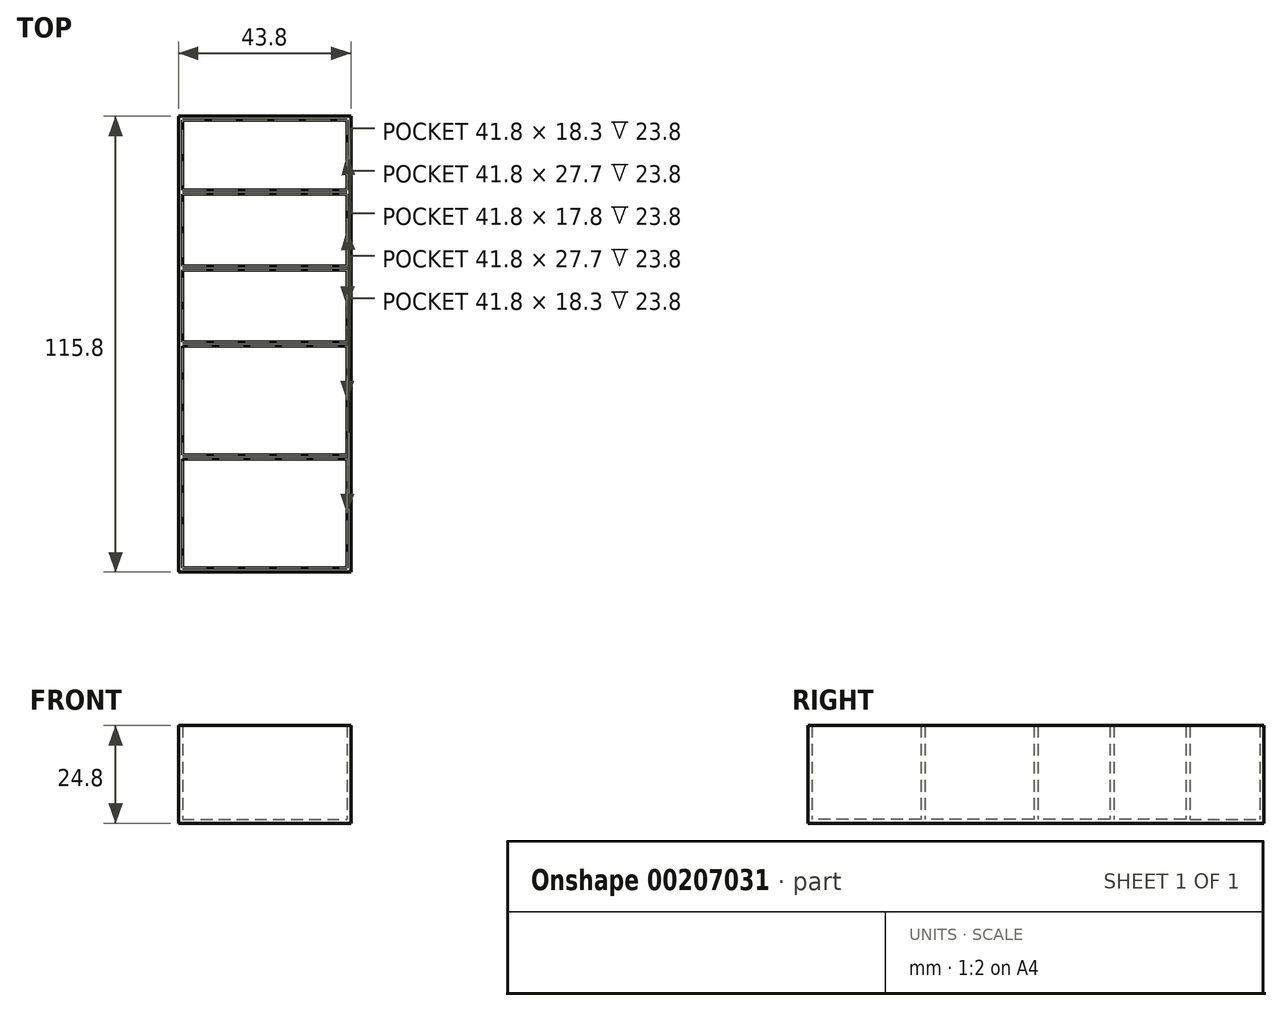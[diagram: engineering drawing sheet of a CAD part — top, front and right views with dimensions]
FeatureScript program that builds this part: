
annotation { "Feature Type Name" : "Feature", "Feature Type Description" : "" }
export const myFeature = defineFeature(function(context is Context, id is Id, definition is map)
    precondition{}
    {
        {
            var Q0;
            Q0=qCreatedBy(makeId("Top.planeOp"),FACE);
            var sketch = newSketch(context, id + "F0", { "sketchPlane" : qUnion([Q0])});
            skLineSegment(sketch, "E0.bottom", {"start": v(0, 0) * mm, "end": v(43.8, 0) * mm});
            skLineSegment(sketch, "E0.top", {"start": v(0, -115.8) * mm, "end": v(43.8, -115.8) * mm});
            skLineSegment(sketch, "E0.left", {"start": v(0, 0) * mm, "end": v(0, -115.8) * mm});
            skLineSegment(sketch, "E0.right", {"start": v(43.8, 0) * mm, "end": v(43.8, -115.8) * mm});
            skSolve(sketch);
        }
        {
            var Q0;
            Q0=makeQuery(id+"F0.imprint","IMPRINT",FACE,{"disambiguationData":[TD([[makeQuery(id+"F0.imprint","IMPRINT",EDGE,{"derivedFrom":sQuery(id+"F0.wireOp",EDGE,"E0.bottom")}),-1.0]])]});
            extrude(context, id + "F1", {"entities" : qUnion([Q0]), "depth" : 1 * mm});
        }
        {
            var Q0;
            Q0=makeQuery(id+"F1.opExtrude","CAP_FACE",FACE,{"disambiguationData":[OSD([sQuery(id+"F0.wireOp",EDGE,"E0.bottom"),sQuery(id+"F0.wireOp",EDGE,"E0.top"),sQuery(id+"F0.wireOp",EDGE,"E0.left"),sQuery(id+"F0.wireOp",EDGE,"E0.right")])],"isStart":false});
            var sketch = newSketch(context, id + "F2", { "sketchPlane" : qUnion([Q0])});
            skLineSegment(sketch, "E1.top", {"start": v(0, -115.8) * mm, "end": v(43.8, -115.8) * mm});
            skLineSegment(sketch, "E2.0", {"start": v(1, -18.8) * mm, "end": v(42.8, -18.8) * mm});
            skLineSegment(sketch, "E3.0", {"start": v(1, -19.8) * mm, "end": v(42.8, -19.8) * mm});
            skLineSegment(sketch, "E4.0", {"start": v(1, -39.1) * mm, "end": v(42.8, -39.1) * mm});
            skLineSegment(sketch, "E5.0", {"start": v(1, -38.1) * mm, "end": v(42.8, -38.1) * mm});
            skLineSegment(sketch, "E6.0", {"start": v(1, -57.4) * mm, "end": v(42.8, -57.4) * mm});
            skLineSegment(sketch, "E7.0", {"start": v(1, -58.4) * mm, "end": v(42.8, -58.4) * mm});
            skLineSegment(sketch, "E8.0", {"start": v(42.8, -1) * mm, "end": v(1, -1) * mm});
            skLineSegment(sketch, "E8.2", {"start": v(1, -114.8) * mm, "end": v(42.8, -114.8) * mm});
            skLineSegment(sketch, "E8.3", {"start": v(1, -1) * mm, "end": v(1, -18.8) * mm});
            skLineSegment(sketch, "E9.trimOffspring", {"start": v(1, -87.35) * mm, "end": v(1, -114.8) * mm});
            skLineSegment(sketch, "E10.trimOffspring", {"start": v(1, -58.4) * mm, "end": v(1, -86.35) * mm});
            skLineSegment(sketch, "E11.trimOffspring", {"start": v(42.8, -57.4) * mm, "end": v(42.8, -39.1) * mm});
            skLineSegment(sketch, "E12.trimOffspring", {"start": v(42.8, -38.1) * mm, "end": v(42.8, -19.8) * mm});
            skLineSegment(sketch, "E13.trimOffspring", {"start": v(1, -39.1) * mm, "end": v(1, -57.4) * mm});
            skLineSegment(sketch, "E14.trimOffspring", {"start": v(1, -19.8) * mm, "end": v(1, -38.1) * mm});
            skLineSegment(sketch, "E15.trimOffspring", {"start": v(42.8, -18.8) * mm, "end": v(42.8, -1) * mm});
            skLineSegment(sketch, "E16.bottom", {"start": v(43.8, -114.8) * mm, "end": v(0, -114.8) * mm});
            skLineSegment(sketch, "E16.top", {"start": v(43.8, -115.8) * mm, "end": v(0, -115.8) * mm});
            skLineSegment(sketch, "E16.left", {"start": v(43.8, -114.8) * mm, "end": v(43.8, -115.8) * mm});
            skLineSegment(sketch, "E16.right", {"start": v(0, -114.8) * mm, "end": v(0, -115.8) * mm});
            skLineSegment(sketch, "E17.left", {"start": v(1, -57.4) * mm, "end": v(1, -58.4) * mm});
            skLineSegment(sketch, "E17.right", {"start": v(42.8, -57.4) * mm, "end": v(42.8, -58.4) * mm});
            skLineSegment(sketch, "E18.left", {"start": v(1, -38.1) * mm, "end": v(1, -39.1) * mm});
            skLineSegment(sketch, "E18.right", {"start": v(42.8, -38.1) * mm, "end": v(42.8, -39.1) * mm});
            skLineSegment(sketch, "E19.left", {"start": v(1, -18.8) * mm, "end": v(1, -19.8) * mm});
            skLineSegment(sketch, "E19.right", {"start": v(42.8, -18.8) * mm, "end": v(42.8, -19.8) * mm});
            skLineSegment(sketch, "E20.bottom", {"start": v(1, -1) * mm, "end": v(42.8, -1) * mm});
            skLineSegment(sketch, "E20.top", {"start": v(1, 0) * mm, "end": v(42.8, 0) * mm});
            skLineSegment(sketch, "E20.left", {"start": v(1, -1) * mm, "end": v(1, 0) * mm});
            skLineSegment(sketch, "E20.right", {"start": v(42.8, -1) * mm, "end": v(42.8, 0) * mm});
            skLineSegment(sketch, "E21.bottom", {"start": v(0, 0) * mm, "end": v(1, 0) * mm});
            skLineSegment(sketch, "E21.top", {"start": v(0, -114.8) * mm, "end": v(1, -114.8) * mm});
            skLineSegment(sketch, "E21.left", {"start": v(0, 0) * mm, "end": v(0, -114.8) * mm});
            skLineSegment(sketch, "E21.right", {"start": v(1, 0) * mm, "end": v(1, -114.8) * mm});
            skLineSegment(sketch, "E22.bottom", {"start": v(42.8, -114.8) * mm, "end": v(43.8, -114.8) * mm});
            skLineSegment(sketch, "E22.top", {"start": v(42.8, 0) * mm, "end": v(43.8, 0) * mm});
            skLineSegment(sketch, "E22.left", {"start": v(42.8, -114.8) * mm, "end": v(42.8, 0) * mm});
            skLineSegment(sketch, "E22.right", {"start": v(43.8, -114.8) * mm, "end": v(43.8, 0) * mm});
            skLineSegment(sketch, "E23.left", {"start": v(1, -58.4) * mm, "end": v(1, -114.8) * mm});
            skLineSegment(sketch, "E24.right", {"start": v(42.8, -58.4) * mm, "end": v(42.8, -114.8) * mm});
            skLineSegment(sketch, "E25.0", {"start": v(42.8, -86.1) * mm, "end": v(1, -86.1) * mm});
            skLineSegment(sketch, "E26.0", {"start": v(42.8, -87.1) * mm, "end": v(1, -87.1) * mm});
            skSolve(sketch);
        }
        {
            var Q0;
            Q0 = qSketchRegion(id + "F2", true);
            var Q1;
            {var subQ11=sQuery(id+"F2.wireOp",EDGE,"E21.bottom");Q1=makeQuery(id+"F2.imprint","IMPRINT",FACE,{"disambiguationData":[TD([[makeQuery(id+"F2.imprint","IMPRINT",EDGE,{"derivedFrom":subQ11}),-1.0]])]});}
            var Q2;
            {var subQ0=sQuery(id+"F2.wireOp",EDGE,"E2.0");Q2=makeQuery(id+"F2.imprint","IMPRINT",FACE,{"disambiguationData":[TD([[makeQuery(id+"F2.imprint","IMPRINT",EDGE,{"derivedFrom":subQ0}),-1.0]])]});}
            var Q3;
            {var subQ0=sQuery(id+"F2.wireOp",EDGE,"E5.0");Q3=makeQuery(id+"F2.imprint","IMPRINT",FACE,{"disambiguationData":[TD([[makeQuery(id+"F2.imprint","IMPRINT",EDGE,{"derivedFrom":subQ0}),-1.0]])]});}
            var Q4;
            {var subQ0=sQuery(id+"F2.wireOp",EDGE,"E6.0");Q4=makeQuery(id+"F2.imprint","IMPRINT",FACE,{"disambiguationData":[TD([[makeQuery(id+"F2.imprint","IMPRINT",EDGE,{"derivedFrom":subQ0}),-1.0]])]});}
            var Q5;
            {var subQ0=sQuery(id+"F2.wireOp",EDGE,"PQgROF91-BTgT-Lykl-vZNl-fqsxZ6deMe2P.bottom");Q5=makeQuery(id+"F2.imprint","IMPRINT",FACE,{"disambiguationData":[TD([[makeQuery(id+"F2.imprint","IMPRINT",EDGE,{"derivedFrom":subQ0}),-1.0]])]});}
            var Q6;
            {var subQ0=sQuery(id+"F2.wireOp",EDGE,"E25.0");Q6=makeQuery(id+"F2.imprint","IMPRINT",FACE,{"disambiguationData":[TD([[makeQuery(id+"F2.imprint","IMPRINT",EDGE,{"derivedFrom":subQ0}),1.0]])]});}
            extrude(context, id + "F3", {"entities" : qUnion([Q0, Q1, Q2, Q3, Q4, Q5, Q6]), "operationType" : NewBodyOperationType.ADD, "depth" : 23.8 * mm});
        }
    });
